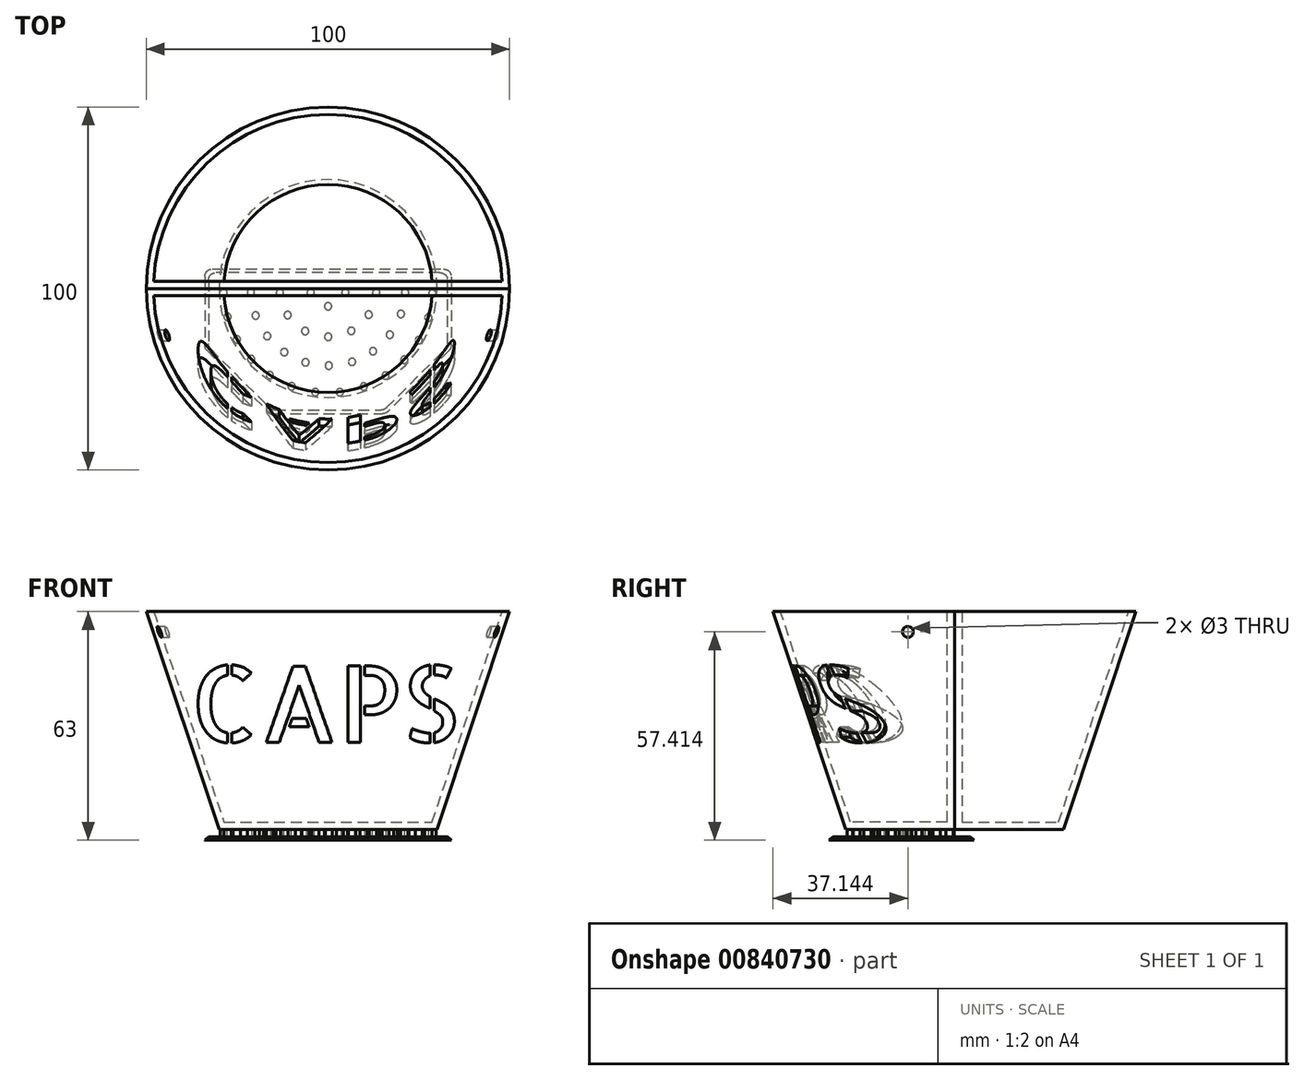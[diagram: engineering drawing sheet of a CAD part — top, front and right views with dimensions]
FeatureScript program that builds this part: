
annotation { "Feature Type Name" : "Feature", "Feature Type Description" : "" }
export const myFeature = defineFeature(function(context is Context, id is Id, definition is map)
    precondition{}
    {
        {
            var Q0;
            Q0=qCreatedBy(makeId("Front.planeOp"),FACE);
            var sketch = newSketch(context, id + "F0", { "sketchPlane" : qUnion([Q0])});
            skLineSegment(sketch, "E0", {"start": v(0, 36) * mm, "end": v(50, 36) * mm});
            skLineSegment(sketch, "E1", {"start": v(50, 36) * mm, "end": v(30, -24) * mm});
            skLineSegment(sketch, "E2", {"start": v(30, -24) * mm, "end": v(0, -24) * mm});
            skLineSegment(sketch, "E3", {"start": v(0, -24) * mm, "end": v(0, 36) * mm});
            skSolve(sketch);
        }
        {
            var Q0;
            Q0=makeQuery(id+"F0.imprint","IMPRINT",FACE,{"disambiguationData":[TD([[makeQuery(id+"F0.imprint","IMPRINT",EDGE,{"derivedFrom":sQuery(id+"F0.wireOp",EDGE,"E0")}),-1.0]])]});
            var Q1;
            Q1=sQuery(id+"F0.wireOp",EDGE,"E3");
            revolve(context, id + "F1", {"surfaceOperationType" : NewSurfaceOperationType.NEW, "entities" : qUnion([Q0]), "axis" : qUnion([Q1]), "revolveType" : RevolveType.ONE_DIRECTION, "angle" : 180 * degree});
        }
        {
            var Q0;
            Q0=makeQuery(id+"F1.opRevolve","SWEPT_FACE",FACE,{"disambiguationData":[OSD([sQuery(id+"F0.wireOp",EDGE,"E2")])]});
            var sketch = newSketch(context, id + "F2", { "sketchPlane" : qUnion([Q0])});
            skArc(sketch, "E4", {"start": v(-28, -2) * mm, "mid": v(0, -28) * mm, "end": v(28, -2) * mm});
            skLineSegment(sketch, "E5", {"start": v(-28, -2) * mm, "end": v(28, -2) * mm});
            skSolve(sketch);
        }
        {
            var Q0;
            Q0=makeQuery(id+"F2.imprint","IMPRINT",FACE,{"disambiguationData":[TD([[makeQuery(id+"F2.imprint","IMPRINT",EDGE,{"derivedFrom":sQuery(id+"F2.wireOp",EDGE,"E4")}),1.0]])]});
            var Q1;
            Q1=makeQuery(id+"F1.opRevolve","SWEPT_FACE",FACE,{"disambiguationData":[OSD([sQuery(id+"F0.wireOp",EDGE,"E0")])]});
            extrude(context, id + "F3", {"entities" : qUnion([Q0]), "operationType" : NewBodyOperationType.REMOVE, "endBound" : BoundingType.UP_TO_SURFACE, "oppositeDirection" : true, "depth" : 25 * mm, "endBoundEntityFace" : qUnion([Q1]), "offsetDistance" : 2 * mm, "hasDraft" : true, "draftAngle" : 18.38 * degree});
        }
        {
            var Q0;
            Q0=makeQuery(id+"F1.opRevolve","SWEPT_FACE",FACE,{"disambiguationData":[OSD([sQuery(id+"F0.wireOp",EDGE,"E0")])]});
            var sketch = newSketch(context, id + "F4", { "sketchPlane" : qUnion([Q0])});
            skLineSegment(sketch, "E6.bottom", {"start": v(-50, 0) * mm, "end": v(49.96, 0) * mm});
            skLineSegment(sketch, "E6.top", {"start": v(-50, 2) * mm, "end": v(49.96, 2) * mm});
            skLineSegment(sketch, "E6.left", {"start": v(-50, 0) * mm, "end": v(-50, 2) * mm});
            skLineSegment(sketch, "E6.right", {"start": v(49.96, 0) * mm, "end": v(49.96, 2) * mm});
            skSolve(sketch);
        }
        {
            var Q0;
            {var subQ0=sQuery(id+"F4.wireOp",EDGE,"E6.bottom");var subQ1=makeQuery(id+"F3.boolean.opBoolean","COPY",EDGE,{"derivedFrom":makeQuery(id+"F3.opExtrude","TWEAK_EDGE",EDGE,{"derivedFrom":[makeQuery(id+"F1.opRevolve","SWEPT_FACE",FACE,{"disambiguationData":[OSD([sQuery(id+"F0.wireOp",EDGE,"E0")])]}),makeQuery(id+"F2.imprint","IMPRINT",EDGE,{"derivedFrom":sQuery(id+"F2.wireOp",EDGE,"E4")})]})});var subQ2=makeQuery(id+"F4.imprint","INTERSECT",VERTEX,{"disambiguationData":[OD(0.0)],"derivedFrom":[subQ1,subQ0]});var subQ3=makeQuery(id+"F4.imprint","INTERSECT",VERTEX,{"disambiguationData":[OD(1.0)],"derivedFrom":[subQ1,subQ0]});Q0=makeQuery(id+"F4.imprint","IMPRINT",FACE,{"disambiguationData":[TD([[makeQuery(id+"F4.imprint","IMPRINT",EDGE,{"disambiguationData":[TD([[subQ2,1.0],[subQ3,-1.0]])],"derivedFrom":subQ0}),1.0]])]});}
            var Q1;
            Q1=makeQuery(id+"F1.opRevolve","SWEPT_FACE",FACE,{"disambiguationData":[OSD([sQuery(id+"F0.wireOp",EDGE,"E2")])]});
            extrude(context, id + "F5", {"entities" : qUnion([Q0]), "operationType" : NewBodyOperationType.ADD, "endBound" : BoundingType.UP_TO_NEXT, "oppositeDirection" : true, "depth" : 25 * mm, "endBoundEntityFace" : qUnion([Q1]), "offsetDistance" : 25 * mm});
        }
        {
            var Q0;
            Q0=makeQuery(id+"F5.boolean.opBoolean","MERGE",FACE,{"derivedFrom":[makeQuery(id+"F1.opRevolve","CAP_FACE",FACE,{"disambiguationData":[OSD([sQuery(id+"F0.wireOp",EDGE,"E0"),sQuery(id+"F0.wireOp",EDGE,"E1"),sQuery(id+"F0.wireOp",EDGE,"E2"),sQuery(id+"F0.wireOp",EDGE,"E3")])],"isStart":true}),makeQuery(id+"F5.opExtrude","SWEPT_FACE",FACE,{"disambiguationData":[OSD([sQuery(id+"F4.wireOp",EDGE,"E6.bottom")])]})]});
            var sketch = newSketch(context, id + "F6", { "sketchPlane" : qUnion([Q0])});
            skLineSegment(sketch, "E7.bottom", {"start": v(-30, -24) * mm, "end": v(30, -24) * mm});
            skLineSegment(sketch, "E7.top", {"start": v(-30, -22) * mm, "end": v(30, -22) * mm});
            skLineSegment(sketch, "E7.left", {"start": v(-30, -24) * mm, "end": v(-30, -22) * mm});
            skLineSegment(sketch, "E7.right", {"start": v(30, -24) * mm, "end": v(30, -22) * mm});
            skSolve(sketch);
        }
        {
            var Q0;
            Q0 = qSketchRegion(id + "F6", true);
            var Q1;
            Q1=makeQuery(id+"F3.boolean.opBoolean","COPY",FACE,{"derivedFrom":makeQuery(id+"F3.opExtrude","SWEPT_FACE",FACE,{"disambiguationData":[OSD([sQuery(id+"F2.wireOp",EDGE,"E4")])]})});
            extrude(context, id + "F7", {"entities" : qUnion([Q0]), "operationType" : NewBodyOperationType.ADD, "endBound" : BoundingType.UP_TO_SURFACE, "oppositeDirection" : true, "depth" : 25 * mm, "endBoundEntityFace" : qUnion([Q1]), "offsetDistance" : 25 * mm});
        }
        {
            var Q0;
            Q0=makeQuery(id+"F1.opRevolve","SWEPT_BODY",BODY,{"disambiguationData":[OSD([sQuery(id+"F0.wireOp",EDGE,"E0"),sQuery(id+"F0.wireOp",EDGE,"E1"),sQuery(id+"F0.wireOp",EDGE,"E2"),sQuery(id+"F0.wireOp",EDGE,"E3")])]});
            var Q1;
            Q1=qCreatedBy(makeId("Front.planeOp"),FACE);
            mirror(context, id + "F8", {"entities" : qUnion([Q0]), "mirrorPlane" : qUnion([Q1])});
        }
        {
            var Q0;
            Q0=qCreatedBy(makeId("Front.planeOp"),FACE);
            cPlane(context, id + "F9", {"entities" : qUnion([Q0]), "cplaneType" : CPlaneType.OFFSET, "offset" : 25 * mm, "width" : 150 * mm, "height" : 150 * mm});
        }
        {
            var Q0;
            Q0=qCreatedBy(id+"F9.planeOp",FACE);
            var sketch = newSketch(context, id + "F10", { "sketchPlane" : qUnion([Q0])});
            skText(sketch, "E8", { "text": "CAPS", "fontName": "AllertaStencil-Regular.ttf"});
            skLineSegment(sketch, "E9", {"start": v(-35.58, 5.87) * mm, "end": v(-39.94, 5.87) * mm});
            skLineSegment(sketch, "E10", {"start": v(34.86, 3.65) * mm, "end": v(39.25, 3.65) * mm});
            const initialGuessF10  = {"E8": [-0.03802, -8e-05, 1, 0, 0.0211]};
            skSetInitialGuess(sketch, initialGuessF10);
            skSolve(sketch);
        }
        {
            var Q0;
            Q0 = qSketchRegion(id + "F10", true);
            extrude(context, id + "F11", {"entities" : qUnion([Q0]), "operationType" : NewBodyOperationType.REMOVE, "endBound" : BoundingType.SYMMETRIC, "oppositeDirection" : true, "depth" : 40 * mm, "offsetDistance" : 25 * mm});
        }
        {
            var Q0;
            Q0=qCreatedBy(makeId("Right.planeOp"),FACE);
            var sketch = newSketch(context, id + "F12", { "sketchPlane" : qUnion([Q0])});
            skCircle(sketch, "E11", {"center": v(-12.86, 30.41) * mm, "radius": 1.5 * mm});
            skSolve(sketch);
        }
        {
            var Q0;
            Q0 = qSketchRegion(id + "F12", true);
            extrude(context, id + "F13", {"entities" : qUnion([Q0]), "operationType" : NewBodyOperationType.REMOVE, "endBound" : BoundingType.SYMMETRIC, "oppositeDirection" : true, "depth" : 100 * mm, "offsetDistance" : 25 * mm});
        }
        {
            var Q0;
            Q0=makeQuery(id+"F8.opPattern","COPY",FACE,{"derivedFrom":makeQuery(id+"F7.boolean.opBoolean","MERGE",FACE,{"derivedFrom":[makeQuery(id+"F1.opRevolve","SWEPT_FACE",FACE,{"disambiguationData":[OSD([sQuery(id+"F0.wireOp",EDGE,"E2")])]}),makeQuery(id+"F7.opExtrude","SWEPT_FACE",FACE,{"disambiguationData":[OSD([sQuery(id+"F6.wireOp",EDGE,"E7.bottom")])]})]}),"instanceName":"1"});
            var sketch = newSketch(context, id + "F14", { "sketchPlane" : qUnion([Q0])});
            skCircle(sketch, "E12", {"center": v(-28.73, 1.15) * mm, "radius": 1 * mm});
            skCircle(sketch, "E13.1.0", {"center": v(-27.68, 7.8) * mm, "radius": 1 * mm});
            skCircle(sketch, "E13.2.0", {"center": v(-25.1, 14.03) * mm, "radius": 1 * mm});
            skCircle(sketch, "E13.3.0", {"center": v(-21.14, 19.5) * mm, "radius": 1 * mm});
            skCircle(sketch, "E13.4.0", {"center": v(-16.03, 23.88) * mm, "radius": 1 * mm});
            skCircle(sketch, "E13.5.0", {"center": v(-10.03, 26.95) * mm, "radius": 1 * mm});
            skCircle(sketch, "E13.6.0", {"center": v(-3.48, 28.55) * mm, "radius": 1 * mm});
            skCircle(sketch, "E13.7.0", {"center": v(3.26, 28.57) * mm, "radius": 1 * mm});
            skCircle(sketch, "E13.8.0", {"center": v(9.82, 27.03) * mm, "radius": 1 * mm});
            skCircle(sketch, "E13.9.0", {"center": v(15.85, 24) * mm, "radius": 1 * mm});
            skCircle(sketch, "E13.10.0", {"center": v(21, 19.65) * mm, "radius": 1 * mm});
            skCircle(sketch, "E13.11.0", {"center": v(25, 14.22) * mm, "radius": 1 * mm});
            skCircle(sketch, "E13.12.0", {"center": v(27.62, 8.01) * mm, "radius": 1 * mm});
            skCircle(sketch, "E13.13.0", {"center": v(28.73, 1.36) * mm, "radius": 1 * mm});
            skPoint(sketch, "E13.center", {"position": v(0, 0) * mm});
            skLineSegment(sketch, "E13.anchor1", {"start": v(0, 0) * mm, "end": v(-28.73, 1.15) * mm, "construction": true});
            skLineSegment(sketch, "E13.anchor2", {"start": v(0, 0) * mm, "end": v(28.73, 1.36) * mm, "construction": true});
            skCircle(sketch, "E14", {"center": v(-21.23, 1.1) * mm, "radius": 1 * mm});
            skCircle(sketch, "E15", {"center": v(-13.26, 1.12) * mm, "radius": 1 * mm});
            skCircle(sketch, "E16", {"center": v(-4.77, 1.1) * mm, "radius": 1 * mm});
            skCircle(sketch, "E17.MirrorC", {"center": v(4.77, 1.1) * mm, "radius": 1 * mm});
            skCircle(sketch, "E18.MirrorC", {"center": v(13.26, 1.12) * mm, "radius": 1 * mm});
            skCircle(sketch, "E19.MirrorC", {"center": v(21.23, 1.1) * mm, "radius": 1 * mm});
            skCircle(sketch, "E20.1.0", {"center": v(-19.91, 7.44) * mm, "radius": 1 * mm});
            skCircle(sketch, "E20.2.0", {"center": v(-16.75, 13.1) * mm, "radius": 1 * mm});
            skCircle(sketch, "E20.3.0", {"center": v(-12.03, 17.53) * mm, "radius": 1 * mm});
            skCircle(sketch, "E20.4.0", {"center": v(-6.2, 20.34) * mm, "radius": 1 * mm});
            skCircle(sketch, "E20.5.0", {"center": v(0.22, 21.26) * mm, "radius": 1 * mm});
            skCircle(sketch, "E20.6.0", {"center": v(6.6, 20.2) * mm, "radius": 1 * mm});
            skCircle(sketch, "E20.7.0", {"center": v(12.39, 17.28) * mm, "radius": 1 * mm});
            skCircle(sketch, "E20.8.0", {"center": v(17.01, 12.75) * mm, "radius": 1 * mm});
            skCircle(sketch, "E20.9.0", {"center": v(20.06, 7.03) * mm, "radius": 1 * mm});
            skLineSegment(sketch, "E20.anchor1", {"start": v(0, 0) * mm, "end": v(-21.23, 1.1) * mm, "construction": true});
            skLineSegment(sketch, "E20.anchor2", {"start": v(0, 0) * mm, "end": v(20.06, 7.03) * mm, "construction": true});
            skCircle(sketch, "E21.1.0", {"center": v(-11.12, 7.3) * mm, "radius": 1 * mm});
            skCircle(sketch, "E21.2.0", {"center": v(-6.3, 11.73) * mm, "radius": 1 * mm});
            skCircle(sketch, "E21.3.0", {"center": v(0.06, 13.3) * mm, "radius": 1 * mm});
            skCircle(sketch, "E21.4.0", {"center": v(6.4, 11.67) * mm, "radius": 1 * mm});
            skCircle(sketch, "E21.5.0", {"center": v(11.2, 7.2) * mm, "radius": 1 * mm});
            skLineSegment(sketch, "E21.anchor1", {"start": v(0, 0) * mm, "end": v(-13.26, 1.12) * mm, "construction": true});
            skLineSegment(sketch, "E21.anchor2", {"start": v(0, 0) * mm, "end": v(11.2, 7.2) * mm, "construction": true});
            skCircle(sketch, "E22.1.0", {"center": v(0.02, 4.9) * mm, "radius": 1 * mm});
            skLineSegment(sketch, "E22.anchor1", {"start": v(0, 0) * mm, "end": v(-4.77, 1.1) * mm, "construction": true});
            skLineSegment(sketch, "E22.anchor2", {"start": v(0, 0) * mm, "end": v(0.02, 4.9) * mm, "construction": true});
            skSolve(sketch);
        }
        {
            var Q0;
            Q0 = qSketchRegion(id + "F14", true);
            extrude(context, id + "F15", {"entities" : qUnion([Q0]), "operationType" : NewBodyOperationType.ADD, "depth" : 2 * mm, "offsetDistance" : 25 * mm});
        }
        {
            var Q0;
            Q0=makeQuery(id+"F15.opExtrude","CAP_FACE",FACE,{"disambiguationData":[OSD([sQuery(id+"F14.wireOp",EDGE,"E13.1.0")])],"isStart":false});
            var sketch = newSketch(context, id + "F16", { "sketchPlane" : qUnion([Q0])});
            skLineSegment(sketch, "E23.bottom", {"start": v(0, -5.35) * mm, "end": v(-33.9, -5.35) * mm});
            skLineSegment(sketch, "E23.top", {"start": v(0, 34.48) * mm, "end": v(-33.9, 34.48) * mm});
            skLineSegment(sketch, "E23.left", {"start": v(0, -5.35) * mm, "end": v(0, 34.48) * mm});
            skLineSegment(sketch, "E23.right", {"start": v(-33.9, -5.35) * mm, "end": v(-33.9, 34.48) * mm});
            skLineSegment(sketch, "E24.MirrorCS", {"start": v(0, 34.48) * mm, "end": v(33.9, 34.48) * mm});
            skLineSegment(sketch, "E25.MirrorCS", {"start": v(33.9, -5.35) * mm, "end": v(33.9, 34.48) * mm});
            skLineSegment(sketch, "E26.MirrorCS", {"start": v(0, -5.35) * mm, "end": v(33.9, -5.35) * mm});
            skSolve(sketch);
        }
        {
            var Q0;
            Q0 = qSketchRegion(id + "F16", true);
            extrude(context, id + "F17", {"entities" : qUnion([Q0]), "operationType" : NewBodyOperationType.ADD, "depth" : 1 * mm, "offsetDistance" : 25 * mm});
        }
        {
            var Q0;
            Q0=makeQuery(id+"F17.opExtrude","SWEPT_EDGE",EDGE,{"disambiguationData":[OSD([sQuery(id+"F16.wireOp",EDGE,"E24.MirrorCS"),sQuery(id+"F16.wireOp",EDGE,"E25.MirrorCS")])]});
            var Q1;
            Q1=makeQuery(id+"F17.opExtrude","SWEPT_EDGE",EDGE,{"disambiguationData":[OSD([sQuery(id+"F16.wireOp",EDGE,"E23.top"),sQuery(id+"F16.wireOp",EDGE,"E23.right")])]});
            chamfer(context, id + "F18", {"entities" : qUnion([Q0, Q1]), "width" : 18 * mm, "tangentPropagation" : true});
        }
        {
            var Q0;
            {var subQ0=sQuery(id+"F16.wireOp",EDGE,"E23.right");var subQ1=sQuery(id+"F16.wireOp",EDGE,"E23.top");Q0=makeQuery(id+"F18.opChamfer","BLEND_EDGE",EDGE,{"blendedFrom":[makeQuery(id+"F17.opExtrude","SWEPT_EDGE",EDGE,{"disambiguationData":[OSD([subQ1,subQ0])]}),makeQuery(id+"F17.opExtrude","CAP_FACE",FACE,{"disambiguationData":[OSD([sQuery(id+"F16.wireOp",EDGE,"E23.bottom"),subQ1,subQ0,sQuery(id+"F16.wireOp",EDGE,"E24.MirrorCS"),sQuery(id+"F16.wireOp",EDGE,"E25.MirrorCS"),sQuery(id+"F16.wireOp",EDGE,"E26.MirrorCS")])],"isStart":true})],"blendedInto":[makeQuery(id+"F17.opExtrude","CAP_FACE",FACE,{"disambiguationData":[OSD([sQuery(id+"F16.wireOp",EDGE,"E23.bottom"),subQ1,subQ0,sQuery(id+"F16.wireOp",EDGE,"E24.MirrorCS"),sQuery(id+"F16.wireOp",EDGE,"E25.MirrorCS"),sQuery(id+"F16.wireOp",EDGE,"E26.MirrorCS")])],"isStart":true})]});}
            var Q1;
            Q1=makeQuery(id+"F17.opExtrude","CAP_EDGE",EDGE,{"disambiguationData":[OSD([sQuery(id+"F16.wireOp",EDGE,"E23.top"),sQuery(id+"F16.wireOp",EDGE,"E24.MirrorCS")])],"isStart":true});
            var Q2;
            Q2=makeQuery(id+"F17.opExtrude","CAP_EDGE",EDGE,{"disambiguationData":[OSD([sQuery(id+"F16.wireOp",EDGE,"E23.right")])],"isStart":true});
            var Q3;
            {var subQ0=sQuery(id+"F16.wireOp",EDGE,"E25.MirrorCS");var subQ1=sQuery(id+"F16.wireOp",EDGE,"E24.MirrorCS");Q3=makeQuery(id+"F18.opChamfer","BLEND_EDGE",EDGE,{"blendedFrom":[makeQuery(id+"F17.opExtrude","SWEPT_EDGE",EDGE,{"disambiguationData":[OSD([subQ1,subQ0])]}),makeQuery(id+"F17.opExtrude","CAP_FACE",FACE,{"disambiguationData":[OSD([sQuery(id+"F16.wireOp",EDGE,"E23.bottom"),sQuery(id+"F16.wireOp",EDGE,"E23.top"),sQuery(id+"F16.wireOp",EDGE,"E23.right"),subQ1,subQ0,sQuery(id+"F16.wireOp",EDGE,"E26.MirrorCS")])],"isStart":true})],"blendedInto":[makeQuery(id+"F17.opExtrude","CAP_FACE",FACE,{"disambiguationData":[OSD([sQuery(id+"F16.wireOp",EDGE,"E23.bottom"),sQuery(id+"F16.wireOp",EDGE,"E23.top"),sQuery(id+"F16.wireOp",EDGE,"E23.right"),subQ1,subQ0,sQuery(id+"F16.wireOp",EDGE,"E26.MirrorCS")])],"isStart":true})]});}
            var Q4;
            Q4=makeQuery(id+"F17.opExtrude","CAP_EDGE",EDGE,{"disambiguationData":[OSD([sQuery(id+"F16.wireOp",EDGE,"E25.MirrorCS")])],"isStart":true});
            var Q5;
            Q5=makeQuery(id+"F17.opExtrude","CAP_EDGE",EDGE,{"disambiguationData":[OSD([sQuery(id+"F16.wireOp",EDGE,"E23.bottom"),sQuery(id+"F16.wireOp",EDGE,"E26.MirrorCS")])],"isStart":true});
            chamfer(context, id + "F19", {"entities" : qUnion([Q0, Q1, Q2, Q3, Q4, Q5]), "width" : 1 * mm, "tangentPropagation" : true});
        }
        {
            var Q0;
            {var subQ0=sQuery(id+"F16.wireOp",EDGE,"E23.right");var subQ1=sQuery(id+"F16.wireOp",EDGE,"E23.top");Q0=makeQuery(id+"F19.opChamfer","BLEND_EDGE",EDGE,{"blendedFrom":[makeQuery(id+"F18.opChamfer","BLEND_EDGE",EDGE,{"blendedFrom":[makeQuery(id+"F17.opExtrude","SWEPT_EDGE",EDGE,{"disambiguationData":[OSD([subQ1,subQ0])]}),makeQuery(id+"F17.opExtrude","CAP_FACE",FACE,{"disambiguationData":[OSD([sQuery(id+"F16.wireOp",EDGE,"E23.bottom"),subQ1,subQ0,sQuery(id+"F16.wireOp",EDGE,"E24.MirrorCS"),sQuery(id+"F16.wireOp",EDGE,"E25.MirrorCS"),sQuery(id+"F16.wireOp",EDGE,"E26.MirrorCS")])],"isStart":true})],"blendedInto":[makeQuery(id+"F17.opExtrude","CAP_FACE",FACE,{"disambiguationData":[OSD([sQuery(id+"F16.wireOp",EDGE,"E23.bottom"),subQ1,subQ0,sQuery(id+"F16.wireOp",EDGE,"E24.MirrorCS"),sQuery(id+"F16.wireOp",EDGE,"E25.MirrorCS"),sQuery(id+"F16.wireOp",EDGE,"E26.MirrorCS")])],"isStart":true})]}),makeQuery(id+"F17.opExtrude","CAP_EDGE",EDGE,{"disambiguationData":[OSD([subQ0])],"isStart":true})],"blendedInto":[]});}
            var Q1;
            {var subQ0=sQuery(id+"F16.wireOp",EDGE,"E24.MirrorCS");var subQ1=sQuery(id+"F16.wireOp",EDGE,"E23.top");var subQ2=sQuery(id+"F16.wireOp",EDGE,"E23.right");Q1=makeQuery(id+"F19.opChamfer","BLEND_EDGE",EDGE,{"blendedFrom":[makeQuery(id+"F18.opChamfer","BLEND_EDGE",EDGE,{"blendedFrom":[makeQuery(id+"F17.opExtrude","SWEPT_EDGE",EDGE,{"disambiguationData":[OSD([subQ1,subQ2])]}),makeQuery(id+"F17.opExtrude","CAP_FACE",FACE,{"disambiguationData":[OSD([sQuery(id+"F16.wireOp",EDGE,"E23.bottom"),subQ1,subQ2,subQ0,sQuery(id+"F16.wireOp",EDGE,"E25.MirrorCS"),sQuery(id+"F16.wireOp",EDGE,"E26.MirrorCS")])],"isStart":true})],"blendedInto":[makeQuery(id+"F17.opExtrude","CAP_FACE",FACE,{"disambiguationData":[OSD([sQuery(id+"F16.wireOp",EDGE,"E23.bottom"),subQ1,subQ2,subQ0,sQuery(id+"F16.wireOp",EDGE,"E25.MirrorCS"),sQuery(id+"F16.wireOp",EDGE,"E26.MirrorCS")])],"isStart":true})]}),makeQuery(id+"F17.opExtrude","CAP_EDGE",EDGE,{"disambiguationData":[OSD([subQ1,subQ0])],"isStart":true})],"blendedInto":[]});}
            var Q2;
            {var subQ0=sQuery(id+"F16.wireOp",EDGE,"E24.MirrorCS");var subQ1=sQuery(id+"F16.wireOp",EDGE,"E23.top");var subQ2=sQuery(id+"F16.wireOp",EDGE,"E25.MirrorCS");Q2=makeQuery(id+"F19.opChamfer","BLEND_EDGE",EDGE,{"blendedFrom":[makeQuery(id+"F18.opChamfer","BLEND_EDGE",EDGE,{"blendedFrom":[makeQuery(id+"F17.opExtrude","SWEPT_EDGE",EDGE,{"disambiguationData":[OSD([subQ0,subQ2])]}),makeQuery(id+"F17.opExtrude","CAP_FACE",FACE,{"disambiguationData":[OSD([sQuery(id+"F16.wireOp",EDGE,"E23.bottom"),subQ1,sQuery(id+"F16.wireOp",EDGE,"E23.right"),subQ0,subQ2,sQuery(id+"F16.wireOp",EDGE,"E26.MirrorCS")])],"isStart":true})],"blendedInto":[makeQuery(id+"F17.opExtrude","CAP_FACE",FACE,{"disambiguationData":[OSD([sQuery(id+"F16.wireOp",EDGE,"E23.bottom"),subQ1,sQuery(id+"F16.wireOp",EDGE,"E23.right"),subQ0,subQ2,sQuery(id+"F16.wireOp",EDGE,"E26.MirrorCS")])],"isStart":true})]}),makeQuery(id+"F17.opExtrude","CAP_EDGE",EDGE,{"disambiguationData":[OSD([subQ1,subQ0])],"isStart":true})],"blendedInto":[]});}
            var Q3;
            {var subQ0=sQuery(id+"F16.wireOp",EDGE,"E25.MirrorCS");var subQ1=sQuery(id+"F16.wireOp",EDGE,"E24.MirrorCS");Q3=makeQuery(id+"F19.opChamfer","BLEND_EDGE",EDGE,{"blendedFrom":[makeQuery(id+"F18.opChamfer","BLEND_EDGE",EDGE,{"blendedFrom":[makeQuery(id+"F17.opExtrude","SWEPT_EDGE",EDGE,{"disambiguationData":[OSD([subQ1,subQ0])]}),makeQuery(id+"F17.opExtrude","CAP_FACE",FACE,{"disambiguationData":[OSD([sQuery(id+"F16.wireOp",EDGE,"E23.bottom"),sQuery(id+"F16.wireOp",EDGE,"E23.top"),sQuery(id+"F16.wireOp",EDGE,"E23.right"),subQ1,subQ0,sQuery(id+"F16.wireOp",EDGE,"E26.MirrorCS")])],"isStart":true})],"blendedInto":[makeQuery(id+"F17.opExtrude","CAP_FACE",FACE,{"disambiguationData":[OSD([sQuery(id+"F16.wireOp",EDGE,"E23.bottom"),sQuery(id+"F16.wireOp",EDGE,"E23.top"),sQuery(id+"F16.wireOp",EDGE,"E23.right"),subQ1,subQ0,sQuery(id+"F16.wireOp",EDGE,"E26.MirrorCS")])],"isStart":true})]}),makeQuery(id+"F17.opExtrude","CAP_EDGE",EDGE,{"disambiguationData":[OSD([subQ0])],"isStart":true})],"blendedInto":[]});}
            var Q4;
            Q4=makeQuery(id+"F19.opChamfer","BLEND_EDGE",EDGE,{"blendedFrom":[makeQuery(id+"F17.opExtrude","CAP_EDGE",EDGE,{"disambiguationData":[OSD([sQuery(id+"F16.wireOp",EDGE,"E23.bottom"),sQuery(id+"F16.wireOp",EDGE,"E26.MirrorCS")])],"isStart":true}),makeQuery(id+"F17.opExtrude","CAP_EDGE",EDGE,{"disambiguationData":[OSD([sQuery(id+"F16.wireOp",EDGE,"E25.MirrorCS")])],"isStart":true})],"blendedInto":[]});
            var Q5;
            Q5=makeQuery(id+"F19.opChamfer","BLEND_EDGE",EDGE,{"blendedFrom":[makeQuery(id+"F17.opExtrude","CAP_EDGE",EDGE,{"disambiguationData":[OSD([sQuery(id+"F16.wireOp",EDGE,"E23.bottom"),sQuery(id+"F16.wireOp",EDGE,"E26.MirrorCS")])],"isStart":true}),makeQuery(id+"F17.opExtrude","CAP_EDGE",EDGE,{"disambiguationData":[OSD([sQuery(id+"F16.wireOp",EDGE,"E23.right")])],"isStart":true})],"blendedInto":[]});
            fillet(context, id + "F20", {"entities" : qUnion([Q0, Q1, Q2, Q3, Q4, Q5]), "radius" : 3 * mm, "tangentPropagation" : true, "allowEdgeOverflow" : false});
        }
    });
